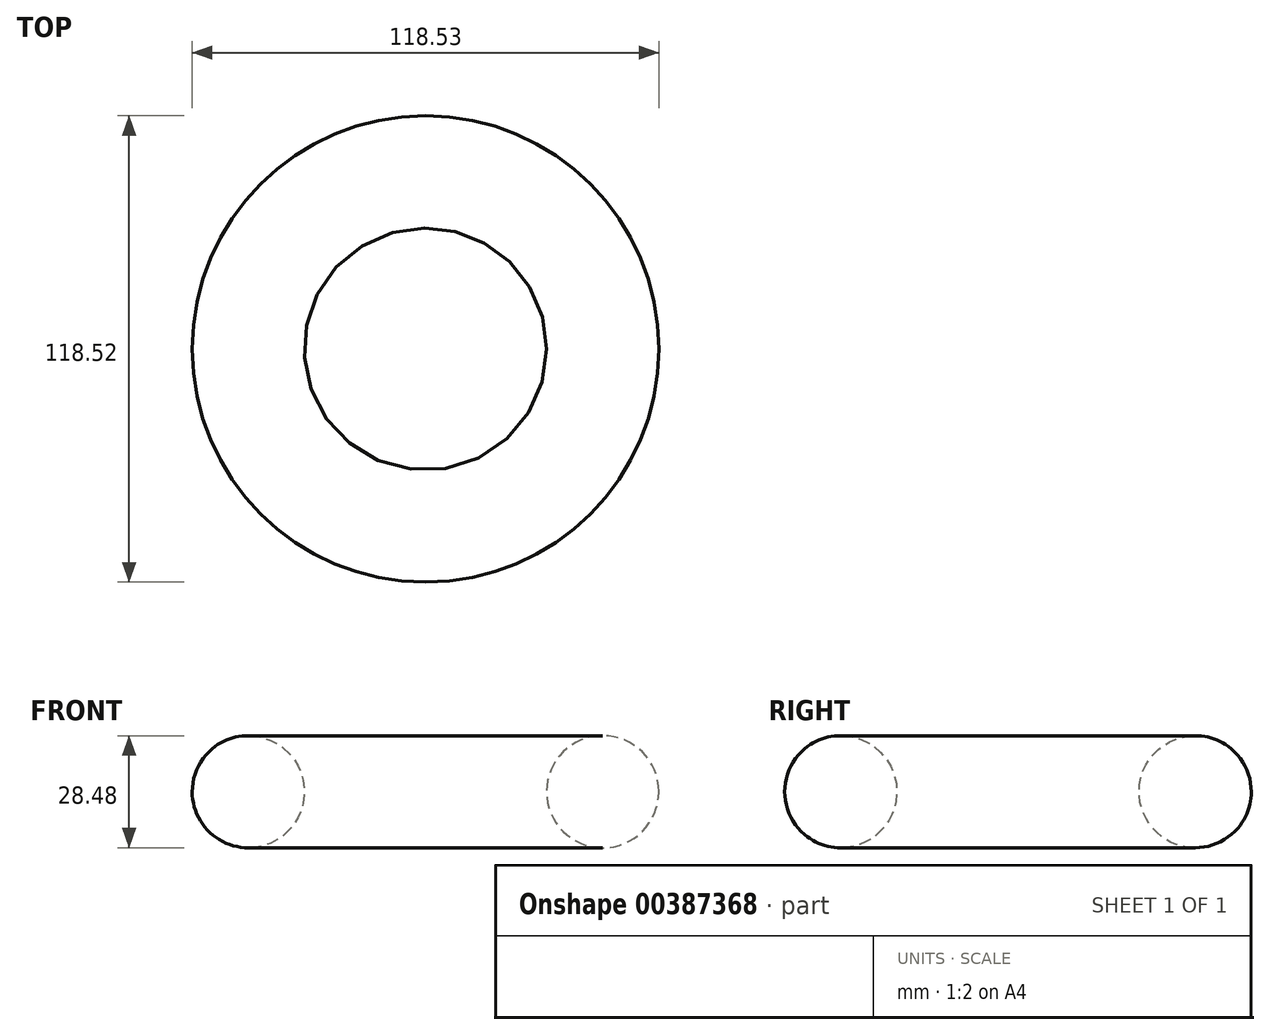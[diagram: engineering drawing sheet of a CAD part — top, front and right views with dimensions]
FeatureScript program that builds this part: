
annotation { "Feature Type Name" : "Feature", "Feature Type Description" : "" }
export const myFeature = defineFeature(function(context is Context, id is Id, definition is map)
    precondition{}
    {
        {
            var Q0;
            Q0=qCreatedBy(makeId("Front.planeOp"),FACE);
            var sketch = newSketch(context, id + "F0", { "sketchPlane" : qUnion([Q0])});
            skLineSegment(sketch, "E0", {"start": v(-27.92, 60.74) * mm, "end": v(-27.92, -42.86) * mm, "construction": true});
            skCircle(sketch, "E1", {"center": v(17.1, 42.46) * mm, "radius": 14.24 * mm});
            skSolve(sketch);
        }
        {
            var Q0;
            Q0=makeQuery(id+"F0.imprint","IMPRINT",FACE,{"disambiguationData":[TD([[makeQuery(id+"F0.imprint","IMPRINT",EDGE,{"derivedFrom":sQuery(id+"F0.wireOp",EDGE,"E1")}),1.0]])]});
            var Q1;
            Q1=sQuery(id+"F0.wireOp",EDGE,"E0");
            revolve(context, id + "F1", {"entities" : qUnion([Q0]), "axis" : qUnion([Q1]), "revolveType" : RevolveType.FULL});
        }
    });
